# Revit family: Vitra-ShowerMixer-SentoSeries-A40699
name_source: partatom
category: Plumbing Fixtures
units: mm (PartAtom-declared; Revit-internal decimal feet)

## family parameters
Always vertical = Yes
Cut with Voids When Loaded = No
Host = Wall
OmniClass Number = 23.45.55.17
OmniClass Title = Mixing Faucets
Part Type = Normal
Room Calculation Point = No
Round Connector Dimension = Use Diameter
Shared = Yes

## types (1)
- ShowerMixerSpout-Vitra-Sento-A40699
    Article No. (default) = A40699
    BIMobject category = Shower Mixer
    CW Connection = No
    CWFU = 0
    Coating Material = Vitra-Chrome
    Color = Chrome
    Connection Diameter (mm) = 20 mm  [stored 0.0656168 ft]
    Cost = 0 $
    Date of publishing = 2019
    Default Elevation = 800 mm  [stored 2.62467 ft]
    Depth (mm) = 200 mm  [stored 0.656168 ft]
    Description = To clean your product use a soft cloth soaked in alcohol or soap. Never use. acid or hydrochloric acid used to clean closed and floor and never use cleaning salt used to clean basin and sink.
    Design country = Turkey
    HW Connection = No
    HWFU = 0
    Height (mm) = 80 mm  [stored 0.262467 ft]
    Hot Water Supply (max.) = 90 °C
    Hot Water temperature, factory set to = 38 °C
    IFC Classification = Sanitary Terminal
    Installation instructions = https://cdn.vitra.com.tr
    Main Material = Brass
    Manufacturer = Vitra
    Manufacturer name = Vitra
    Masterformat 2014 Code = 22 40 00
    Masterformat 2014 Description = Plumbing Fixtures
    Min. flow pressure of = 0.5 bar
    Model = A40699
    MountingType = Wall-mounted
    NBS Reference Code = 45-35-70/315
    NBS Reference Description = Water supply fittings for baths
    Nominal Height = 0 mm  [stored 0 ft]
    Nominal Length = 0 mm  [stored 0 ft]
    Nominal Width = 0 mm  [stored 0 ft]
    Number Of Connections = 1
    OmniClass Code = 23.45.55.17
    OmniClass Description = Mixing Faucets
    Product Guid = https://cdn.vitra.com.tr
    Product SKU = A40699
    Product Type = Shower Mixer
    Product certification = https://vitraglobal.com
    Product data url = https://vitraglobal.com
    Product family = Sento
    Product group = Sento Shower Mixer Spout
    Range of Hot Water Supply = 5 - 65 °C
    Range of flow pressure = 1 - 5 bar
    Spares Availability Duration = 10 Years
    Technical description = https://vitraglobal.com
    Test Pressure = 16 bar
    UNSPSC Code = 301815
    URL = https://vitraglobal.com
    Uniclass 1.4 Code = L725111
    Uniclass 1.4 Description = Mixer taps
    Uniclass 2.0 Code = Pr_40_20_87_09
    Uniclass 2.0 Description = Bath taps
    Uniclass 2015 Code = Pr_40_20_87_09
    Uniclass 2015 Name = Bath taps
    Uniformat II Code = 22 40 00
    Uniformat II Description = Plumbing Fixture
    WFU = 0
    Weight Net (Kg) = 0,935
    Width (mm) = 80 mm  [stored 0.262467 ft]
    Youtube = https://www.youtube.com

note: [stored X ft] marks values corroborated as IEEE doubles in the binary element streams (Revit-internal decimal feet)

## geometry (parser evidence)
native form markers: Sweep x3
no freeform markers — native parametric forms only
